# Revit family: PUHY-EM500YNW-A1
name_source: partatom
category: 機械設備
revit_build: Autodesk Revit 2016 (Build: 20150220_1215(x64)
units: mm (PartAtom-declared; Revit-internal decimal feet)

## family parameters
OmniClass タイトル = Climate Control (HVAC)
OmniClass 番号 = 23.75.00.00
パーツ タイプ = 標準
ロード時にボイドで切り取り = いいえ
丸型コネクタ寸法 = 半径を使用
作業面に基づく = いいえ
共有 = いいえ
常に垂直 = はい
部屋の計算ポイント = いいえ

## types (6) — shared parameters
Airflow Rate (m3/h) = 21900
Airflow Rate (m3/min) = 365
Compressor Motor Output (kW) = 12.9
Compressor_Lubricant = MEL46EH
Compressor_Quantity = 1
Compressor_Type = Inverter scroll hermetic compressor
Cooling Capacity (kW) = 56
Cooling EER (kW/kW) = 3.28
Cooling Power Input (kW) = 17.07
Depth = 740  [stored 2.42782 ft]
External Finish = Pre-coated galvanized steel sheets (+powder coating for -BS type) <MUNSELL 5Y 8/1 or similar>
Fan Motor Output (kW) = 1.84
Fan_Quantity = 2
Fan_Type = Propeller Fan
Gas pipe_radius = 14.29  [stored 0.0468832 ft]
Heating COP (kW/kW) = 3.76
Heating Capacity (kW) = 63
Heating Power Input (kW) = 16.75
Height = 1858
Indoor Unit Model/Quantity = W10 to W125/1 to 43
Indoor Unit Total Capacity = 50 to 130% of outdoor unit capacity
Liquid pipe_radius = 7.94  [stored 0.0260499 ft]
Maximum Circuit Ampacity (A) = 44.4
Note_1 = Refrigerant pipe diameters may change depending on the installation condition. Please refer to the installation manual.
Outdoor unit Breaker size (A) = 60
Phase = 3
Protection Devices_High pressure (MPa) = High pressure sensor, High pressure switch at 4.15
Protection Devices_Inverter circuit (COMP./FAN) = Over-heat protection, Over-current protection
Refrigerant Charge (kg) = 10.8
Refrigerant type = R32
Sound Pressure Level (dB(A)) Cooling mode = 63.5
Sound Pressure Level (dB(A)) Heating mode = 66.5
Space View = はい
Subcategory = HVAC
Temp. range of cooling (Indoor temp.) (W.B.) = 15.0 to 24.0
Temp. range of cooling (Outdoor temp.) (D.B.) = -5.0 to 52.0
Temp. range of heating (Indoor temp.) (D.B.) = 15.0 to 27.0
Temp. range of heating (Outdoor temp.) (W.B.) = -20.0 to 15.5
URL = http://www.mitsubishielectric.com
Unit Weight (kg) = 338
Width = 1750  [stored 5.74147 ft]
モデル = PUHY-EM500YNW-A1
製造元 = Mitsubishi Electric Corporation
zero-valued in all types: Equip_No., External static pressure (Pa), SerialNumber, TagNumber

## per-type parameters (varying)
| type | Cooling Current (A) | Heating Current (A) | Hertz | Rated Load Ampacity (A) Cooling mode | Rated Load Ampacity (A) Heating mode | Voltage |
| PUHY-EM500YNW-A1_380V_50Hz | 28.8 | 28.2 | 50 Hz | 28.8 | 28.2 | 380 V |
| PUHY-EM500YNW-A1_380V_60Hz | 28.8 | 28.2 | 60 Hz | 28.8 | 28.2 | 380 V |
| PUHY-EM500YNW-A1_400V_50Hz | 27.3 | 26.8 | 50 Hz | 27.3 | 26.8 | 400 V |
| PUHY-EM500YNW-A1_400V_60Hz | 27.3 | 26.8 | 60 Hz | 27.3 | 26.8 | 400 V |
| PUHY-EM500YNW-A1_415V_50Hz | 26.3 | 25.8 | 50 Hz | 26.3 | 25.8 | 415 V |
| PUHY-EM500YNW-A1_415V_60Hz | 26.3 | 25.8 | 60 Hz | 26.3 | 25.8 | 415 V |

note: [stored X ft] marks values corroborated as IEEE doubles in the binary element streams (Revit-internal decimal feet)

## geometry (parser evidence)
native form markers: Blend x72, Sweep x3
no freeform markers — native parametric forms only
